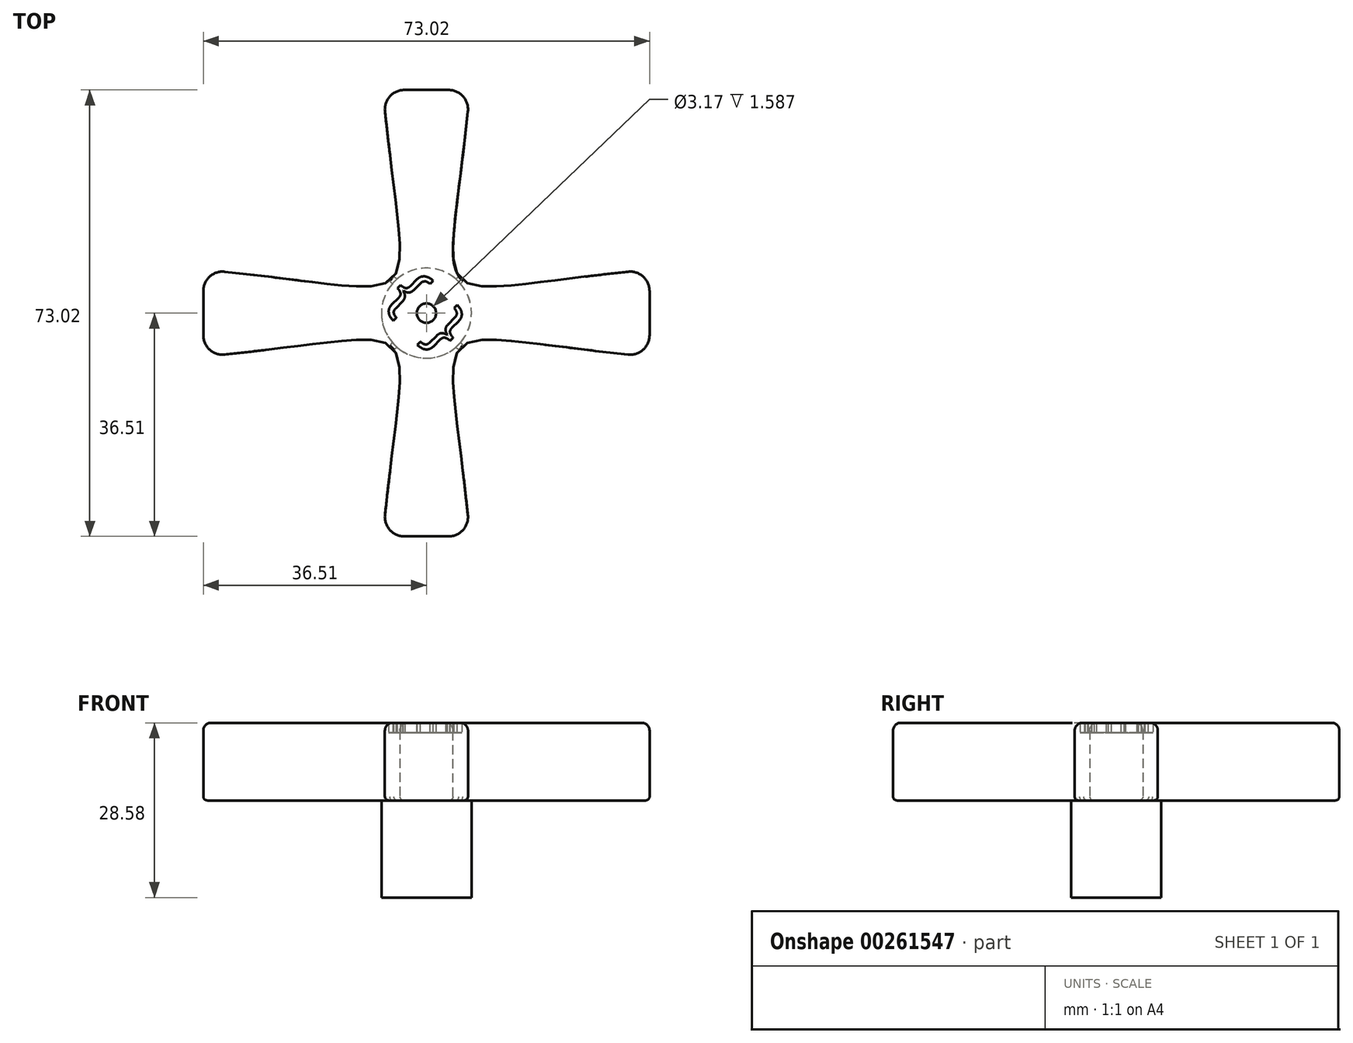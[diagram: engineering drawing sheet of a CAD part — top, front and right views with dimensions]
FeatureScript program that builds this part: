
annotation { "Feature Type Name" : "Feature", "Feature Type Description" : "" }
export const myFeature = defineFeature(function(context is Context, id is Id, definition is map)
    precondition{}
    {
        {
            var Q0;
            Q0=qCreatedBy(makeId("Top.planeOp"),FACE);
            var sketch = newSketch(context, id + "F0", { "sketchPlane" : qUnion([Q0])});
            skLineSegment(sketch, "E0", {"start": v(0, 0) * mm, "end": v(0, 36.51) * mm, "construction": true});
            skLineSegment(sketch, "E1", {"start": v(-36.51, 0) * mm, "end": v(0, 0) * mm, "construction": true});
            skLineSegment(sketch, "E2", {"start": v(36.51, 0) * mm, "end": v(0, 0) * mm, "construction": true});
            skLineSegment(sketch, "E3", {"start": v(0, -36.51) * mm, "end": v(0, 0) * mm, "construction": true});
            skLineSegment(sketch, "E4", {"start": v(-36.51, 7.14) * mm, "end": v(-36.51, -7.14) * mm});
            skLineSegment(sketch, "E5", {"start": v(-7.14, -36.51) * mm, "end": v(7.14, -36.51) * mm});
            skLineSegment(sketch, "E6", {"start": v(36.51, -7.14) * mm, "end": v(36.51, 7.14) * mm});
            skLineSegment(sketch, "E7", {"start": v(-7.14, 36.51) * mm, "end": v(7.14, 36.51) * mm});
            skCircle(sketch, "E8", {"center": v(0, 0) * mm, "radius": 15.88 * mm, "construction": true});
            skLineSegment(sketch, "E9", {"start": v(-15.88, 5.08) * mm, "end": v(-15.88, -5.08) * mm, "construction": true});
            skCircle(sketch, "E10", {"center": v(0, 0) * mm, "radius": 7.94 * mm, "construction": true});
            skLineSegment(sketch, "E11", {"start": v(-5.08, -15.88) * mm, "end": v(5.08, -15.88) * mm, "construction": true});
            skLineSegment(sketch, "E12.MirrorCS", {"start": v(0, 0) * mm, "end": v(0, -36.51) * mm, "construction": true});
            skLineSegment(sketch, "E13", {"start": v(-5.61, -5.61) * mm, "end": v(5.61, 5.61) * mm, "construction": true});
            skFitSpline(sketch, "E14", {"points": [v(-36.51, -7.14) * mm, v(-5.61, -5.61) * mm, v(-7.14, -36.51) * mm], "startDerivative": vector(123.83, 12.38) * mm, "endDerivative": vector(-12.38, -123.83) * mm});
            skFitSpline(sketch, "E15.MirrorCS", {"points": [v(36.51, -7.14) * mm, v(5.61, -5.61) * mm, v(7.14, -36.51) * mm], "startDerivative": vector(-123.83, 12.38) * mm, "endDerivative": vector(12.38, -123.83) * mm});
            skFitSpline(sketch, "E16.MirrorCS", {"points": [v(-36.51, 7.14) * mm, v(-5.61, 5.61) * mm, v(-7.14, 36.51) * mm], "startDerivative": vector(123.83, -12.38) * mm, "endDerivative": vector(-12.38, 123.83) * mm});
            skFitSpline(sketch, "E17.MirrorCS", {"points": [v(36.51, 7.14) * mm, v(5.61, 5.61) * mm, v(7.14, 36.51) * mm], "startDerivative": vector(-123.83, -12.38) * mm, "endDerivative": vector(12.38, 123.83) * mm});
            skSolve(sketch);
        }
        {
            var Q0;
            Q0 = qSketchRegion(id + "F0", true);
            extrude(context, id + "F1", {"entities" : qUnion([Q0]), "depth" : 12.7 * mm});
        }
        {
            var Q0;
            Q0=makeQuery(id+"F1.opExtrude","CAP_FACE",FACE,{"disambiguationData":[OSD([sQuery(id+"F0.wireOp",EDGE,"E4"),sQuery(id+"F0.wireOp",EDGE,"E5"),sQuery(id+"F0.wireOp",EDGE,"E6"),sQuery(id+"F0.wireOp",EDGE,"E7"),sQuery(id+"F0.wireOp",EDGE,"E14"),sQuery(id+"F0.wireOp",EDGE,"E15.MirrorCS"),sQuery(id+"F0.wireOp",EDGE,"E16.MirrorCS"),sQuery(id+"F0.wireOp",EDGE,"E17.MirrorCS")])],"isStart":true});
            var sketch = newSketch(context, id + "F2", { "sketchPlane" : qUnion([Q0])});
            skCircle(sketch, "E18", {"center": v(0, 0) * mm, "radius": 7.37 * mm});
            skSolve(sketch);
        }
        {
            var Q0;
            Q0 = qSketchRegion(id + "F2", true);
            extrude(context, id + "F3", {"entities" : qUnion([Q0]), "operationType" : NewBodyOperationType.ADD, "depth" : 15.88 * mm});
        }
        {
            var Q0;
            Q0=makeQuery(id+"FHBKJaG82kfliYF_1.boolean.opBoolean","MERGE",FACE,{"derivedFrom":[makeQuery(id+"F1.opExtrude","CAP_FACE",FACE,{"disambiguationData":[OSD([sQuery(id+"F0.wireOp",EDGE,"E4"),sQuery(id+"F0.wireOp",EDGE,"E5"),sQuery(id+"F0.wireOp",EDGE,"E6"),sQuery(id+"F0.wireOp",EDGE,"E7"),sQuery(id+"F0.wireOp",EDGE,"E14"),sQuery(id+"F0.wireOp",EDGE,"E15.MirrorCS"),sQuery(id+"F0.wireOp",EDGE,"E16.MirrorCS"),sQuery(id+"F0.wireOp",EDGE,"E17.MirrorCS")])],"isStart":false}),makeQuery(id+"FHBKJaG82kfliYF_1.opExtrude","CAP_FACE",FACE,{"disambiguationData":[OSD([sQuery(id+"FlcRGu9XOME26Uw_1.wireOp",EDGE,"4aeb7ee9-712b-4c87-8b6b-3736a43f95a2"),sQuery(id+"FlcRGu9XOME26Uw_1.wireOp",EDGE,"5124bdd7-5500-46ca-ada0-c6f18179f70a0.MirrorCS"),sQuery(id+"FlcRGu9XOME26Uw_1.wireOp",EDGE,"3c1a6850-1179-4b00-b570-ccdac5f7884b0.MirrorCS"),sQuery(id+"FlcRGu9XOME26Uw_1.wireOp",EDGE,"ff6566bc-f724-427d-8e95-42f8fa4ef3770.MirrorCS"),sQuery(id+"FlcRGu9XOME26Uw_1.wireOp",EDGE,"qXK4DlwG-7KnT-G8Oz-TqMb-Z13vw5oB3guk"),sQuery(id+"FlcRGu9XOME26Uw_1.wireOp",EDGE,"dqaNWhFM-M3ve-srLk-W5Z1-zQcwXBHqWryK"),sQuery(id+"FlcRGu9XOME26Uw_1.wireOp",EDGE,"r9uwT2Yu-TUu2-pDg3-xqRF-IJZkSwj9vNKo"),sQuery(id+"FlcRGu9XOME26Uw_1.wireOp",EDGE,"dcotBPHB-oE0p-CpJw-bHCk-VDZde19CIVf2")])],"isStart":true})]});
            var sketch = newSketch(context, id + "F4", { "sketchPlane" : qUnion([Q0])});
            skText(sketch, "E19", { "text": "{", "fontName": "OpenSans-Regular.ttf"});
            skText(sketch, "E20", { "text": "}", "fontName": "OpenSans-Regular.ttf"});
            skLineSegment(sketch, "E21", {"start": v(-3.74, -0.57) * mm, "end": v(-0.57, -3.74) * mm, "construction": true});
            skLineSegment(sketch, "E22", {"start": v(-2.16, -2.16) * mm, "end": v(9.66, 9.66) * mm, "construction": true});
            skLineSegment(sketch, "E23", {"start": v(-2.81, 2.74) * mm, "end": v(3.1, -3.17) * mm, "construction": true});
            skCircle(sketch, "E24", {"center": v(0, 0) * mm, "radius": 1.59 * mm});
            skLineSegment(sketch, "E25", {"start": v(0, 0) * mm, "end": v(36.51, 0) * mm, "construction": true});
            skLineSegment(sketch, "E26", {"start": v(0, 0) * mm, "end": v(0, -36.51) * mm, "construction": true});
            const initialGuessF4  = {"E19": [-0.0068, 0.0025, 0.7071, -0.7071, 0.00762], "E20": [-0.00057, -0.00374, 0.7071, -0.7071, 0.00762]};
            skSetInitialGuess(sketch, initialGuessF4);
            skSolve(sketch);
        }
        {
            var Q0;
            Q0 = qSketchRegion(id + "F4", true);
            extrude(context, id + "F5", {"entities" : qUnion([Q0]), "operationType" : NewBodyOperationType.REMOVE, "oppositeDirection" : true, "depth" : 1.59 * mm});
        }
        {
            var Q0;
            Q0=makeQuery(id+"F1.opExtrude","SWEPT_EDGE",EDGE,{"disambiguationData":[OSD([sQuery(id+"F0.wireOp",EDGE,"E5"),sQuery(id+"F0.wireOp",EDGE,"E15.MirrorCS")])]});
            var Q1;
            Q1=makeQuery(id+"F1.opExtrude","SWEPT_EDGE",EDGE,{"disambiguationData":[OSD([sQuery(id+"F0.wireOp",EDGE,"E6"),sQuery(id+"F0.wireOp",EDGE,"E15.MirrorCS")])]});
            var Q2;
            Q2=makeQuery(id+"F1.opExtrude","SWEPT_EDGE",EDGE,{"disambiguationData":[OSD([sQuery(id+"F0.wireOp",EDGE,"E6"),sQuery(id+"F0.wireOp",EDGE,"E17.MirrorCS")])]});
            var Q3;
            Q3=makeQuery(id+"F1.opExtrude","SWEPT_EDGE",EDGE,{"disambiguationData":[OSD([sQuery(id+"F0.wireOp",EDGE,"E7"),sQuery(id+"F0.wireOp",EDGE,"E17.MirrorCS")])]});
            var Q4;
            Q4=makeQuery(id+"F1.opExtrude","SWEPT_EDGE",EDGE,{"disambiguationData":[OSD([sQuery(id+"F0.wireOp",EDGE,"E7"),sQuery(id+"F0.wireOp",EDGE,"E16.MirrorCS")])]});
            var Q5;
            Q5=makeQuery(id+"F1.opExtrude","SWEPT_EDGE",EDGE,{"disambiguationData":[OSD([sQuery(id+"F0.wireOp",EDGE,"E4"),sQuery(id+"F0.wireOp",EDGE,"E14")])]});
            var Q6;
            Q6=makeQuery(id+"F1.opExtrude","SWEPT_EDGE",EDGE,{"disambiguationData":[OSD([sQuery(id+"F0.wireOp",EDGE,"E4"),sQuery(id+"F0.wireOp",EDGE,"E16.MirrorCS")])]});
            var Q7;
            Q7=makeQuery(id+"F1.opExtrude","SWEPT_EDGE",EDGE,{"disambiguationData":[OSD([sQuery(id+"F0.wireOp",EDGE,"E5"),sQuery(id+"F0.wireOp",EDGE,"E14")])]});
            fillet(context, id + "F6", {"entities" : qUnion([Q0, Q1, Q2, Q3, Q4, Q5, Q6, Q7]), "radius" : 3.17 * mm, "tangentPropagation" : true, "allowEdgeOverflow" : false});
        }
        {
            var Q0;
            Q0=makeQuery(id+"F1.opExtrude","CAP_EDGE",EDGE,{"disambiguationData":[OSD([sQuery(id+"F0.wireOp",EDGE,"E14")])],"isStart":false});
            fillet(context, id + "F7", {"entities" : qUnion([Q0]), "radius" : 1.27 * mm, "tangentPropagation" : true, "allowEdgeOverflow" : false});
        }
        {
            var Q0;
            Q0=makeQuery(id+"F1.opExtrude","CAP_EDGE",EDGE,{"disambiguationData":[OSD([sQuery(id+"F0.wireOp",EDGE,"E16.MirrorCS")])],"isStart":true});
            fillet(context, id + "F8", {"entities" : qUnion([Q0]), "radius" : 0.64 * mm, "tangentPropagation" : true, "allowEdgeOverflow" : false});
        }
    });
